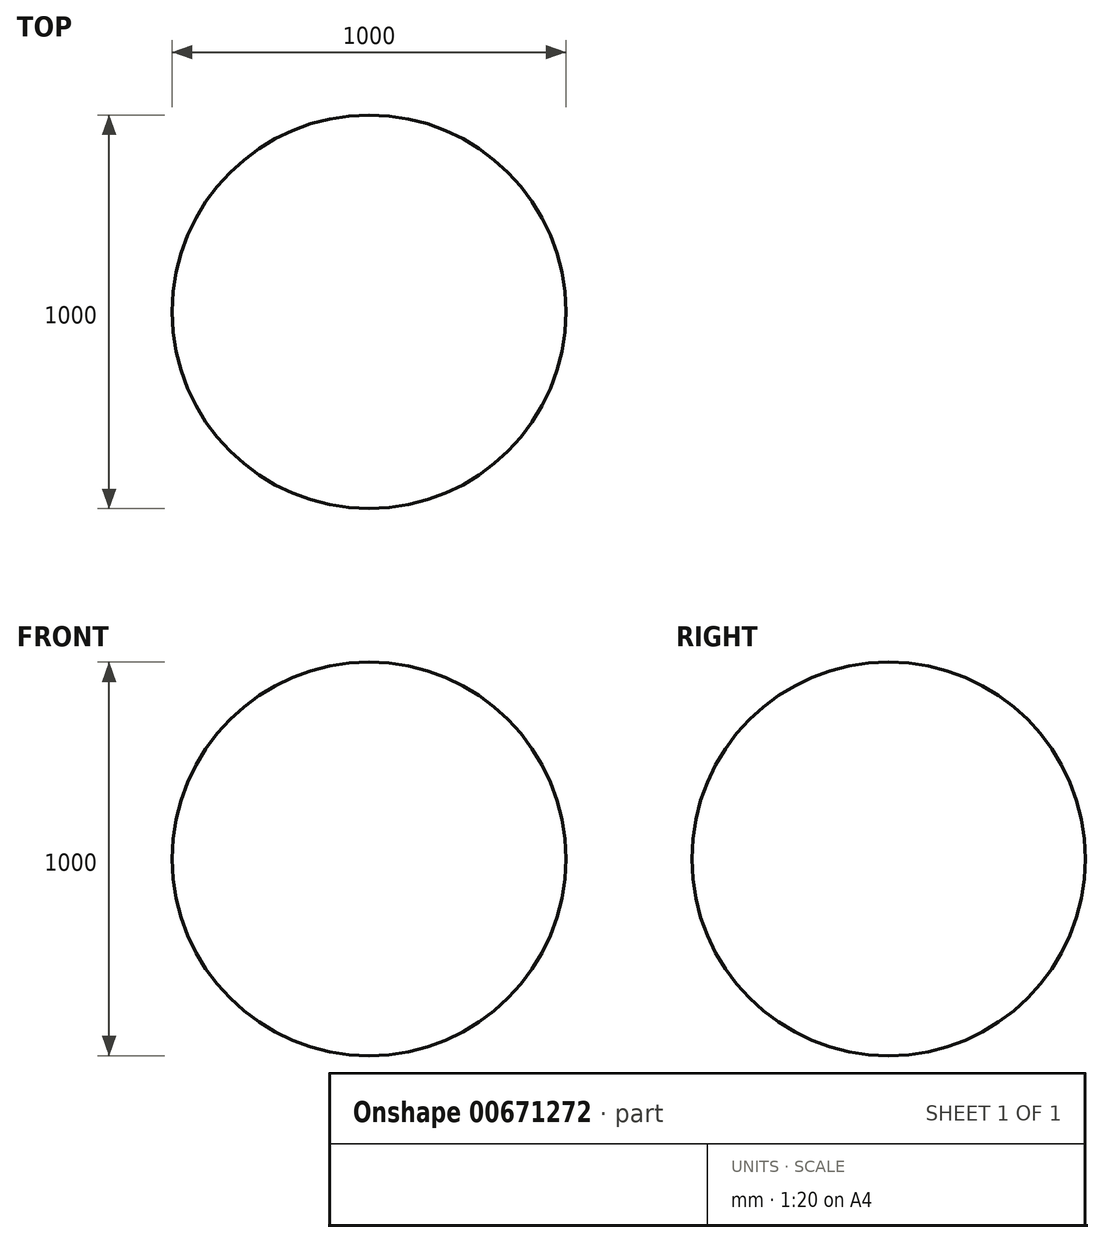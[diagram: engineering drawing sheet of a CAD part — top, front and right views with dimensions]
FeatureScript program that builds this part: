
annotation { "Feature Type Name" : "Feature", "Feature Type Description" : "" }
export const myFeature = defineFeature(function(context is Context, id is Id, definition is map)
    precondition{}
    {
        {
            var Q0;
            Q0=qCreatedBy(makeId("Front.planeOp"),FACE);
            var sketch = newSketch(context, id + "F0", { "sketchPlane" : qUnion([Q0])});
            skCircle(sketch, "E0", {"center": v(0, 0) * mm, "radius": 500 * mm});
            skLineSegment(sketch, "E1", {"start": v(0, 500) * mm, "end": v(0, -500) * mm});
            skSolve(sketch);
        }
        {
            var Q0;
            {var subQ0=sQuery(id+"F0.wireOp",EDGE,"E1");Q0=makeQuery(id+"F0.imprint","IMPRINT",FACE,{"disambiguationData":[TD([[makeQuery(id+"F0.imprint","IMPRINT",EDGE,{"derivedFrom":subQ0}),1.0]])]});}
            var Q1;
            Q1 = qSketchRegion(id + "F2", true);
            var Q2;
            Q2=sQuery(id+"F0.wireOp",EDGE,"E1");
            revolve(context, id + "F1", {"entities" : qUnion([Q0, Q1]), "axis" : qUnion([Q2]), "revolveType" : RevolveType.FULL});
        }
    });
